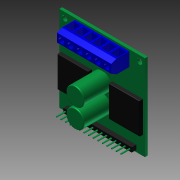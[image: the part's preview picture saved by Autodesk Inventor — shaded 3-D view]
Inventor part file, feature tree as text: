
AUTODESK INVENTOR PART (.ipt)
format: ipt  version: 2012 (Build 160160000, 160)  size: 427,520 bytes
history: native  units: in
note: dims shown in document units (in); Inventor stores cm internally (conversion verified against a paired STEP export)
features: extrude x9, fillet x3, sketch x2, chamfer x2
ambient origin geometry x8: Origin, YZ Plane, XZ Plane, XY Plane, X Axis, Y Axis, Z Axis, Center Point
bodies: Solid1 (feature_tree)
feature tree (16):
  sketch  "Sketch1"  dims[d0=1.86in d1=1.86in]
  extrude  "Extrusion1"  Depth=1.86in
  extrude  "Extrusion2"  Depth=0.1181in
  extrude  "Extrusion3"  Depth=0.1181in
  extrude  "Extrusion4"  Depth=0.1181in
  extrude  "Extrusion5"  Depth=0.1181in
  extrude  "Extrusion6"  Depth=0.1181in
  fillet  "Fillet1"  Radius=1.1811in
  fillet  "Fillet2"  Radius=0.3937in
  chamfer  "Chamfer1"  Distance=0.3937in
  chamfer  "Chamfer2"  Distance=0.3394in
  extrude  "Extrusion7"  Depth=0.0394in
  extrude  "Extrusion8"  Depth=0.2953in
  extrude  "Extrusion9"  Depth=1.4843in
  fillet  "Fillet3"  Radius=0.188in
  sketch  "Sketch2"  dims[d2=0.1181in d3=0.1181in d4=0.1181in d5=0.1181in d6=0.1181in d7=0.1181in d8=1.1811in d9=0.3937in d10=0.3937in d11=0.3394in d12=0.0394in d13=0.2953in d14=1.4843in d15=0.188in d16=0.6693in d17=0.6693in d18=0.6693in d19=0.6693in d20=0.7874in d21=0.7874in d23=0.0197in d24=0.0197in d25=0.0197in d26=0.0197in d27=0.0197in d28=0.0197in d29=0.0197in d30=0.0197in d31=0.0197in d32=0.0197in d33=0.0197in d34=0.0197in d35=0.0197in d36=0.0197in d37=0.0197in d38=0.0197in d39=0.0197in d40=0.0197in d41=0.0197in d42=0.0197in d43=0.0197in d44=0.0197in d45=0.0197in d46=0.0197in d47=0.0197in d48=0.0197in d49=0.0197in d50=0.0197in d51=0.0197in d52=0.0197in d53=0.0325in d54=0.1in d55=0.1in d56=0.1in d57=0.1in d58=0.1in d59=0.1in d60=0.1in d61=0.1in d62=0.1in d63=0.1in d64=0.1in d65=0.1in d66=0.1in d67=0.0999in d68=0.0394in d69=0.0394in d70=0.3937in d71=0.3937in d72=0.1181in d73=0.1181in d74=0.1181in d75=0.1181in d76=0.1181in d77=0.1181in d78=0.041in d79=0.041in d80=0.041in d81=0.041in d82=0.041in d83=0.041in d84=0.0984in d85=0.0in d86=0.2953in d87=0.0in d88=0.0984in d89=0.0395in d90=0.0395in d91=0.0395in d92=0.0395in d93=0.0395in d94=0.0395in d95=0.0395in d96=0.0395in d97=0.0395in d98=0.0395in d99=0.0395in d100=0.0395in d101=0.0395in d102=0.0395in d103=0.0395in d104=0.2643in d105=0.0787in d106=0.0in d107=0.3937in d108=0.0in d109=0.2953in d110=0.0in d111=0.5906in d112=0.0in d113=0.02in d114=0.01in d115=0.07in d116=0.125in d117=60.0deg d118=0.04in d119=0.125in d120=0.481in d121=0.0394in d122=0.0394in d123=0.0394in d124=0.0394in d125=0.0394in d126=0.1575in d127=0.1575in d128=0.1575in d129=0.1575in d130=0.1575in d131=0.1575in d132=0.1969in d133=0.1969in d134=0.1969in d135=0.1969in d136=0.1969in d137=0.1969in d138=0.0435in d139=0.0435in d140=0.0435in d141=0.0435in d142=0.0435in d143=0.0435in d144=0.0197in d145=0.2362in d146=0.0in d147=0.063in d148=0.0in d149=0.2362in d150=0.2362in d151=0.2362in d152=0.2362in d153=0.5118in d154=0.6693in d155=0.0394in d156=0.0394in d157=0.0984in d158=0.0in d159=0.01in]
